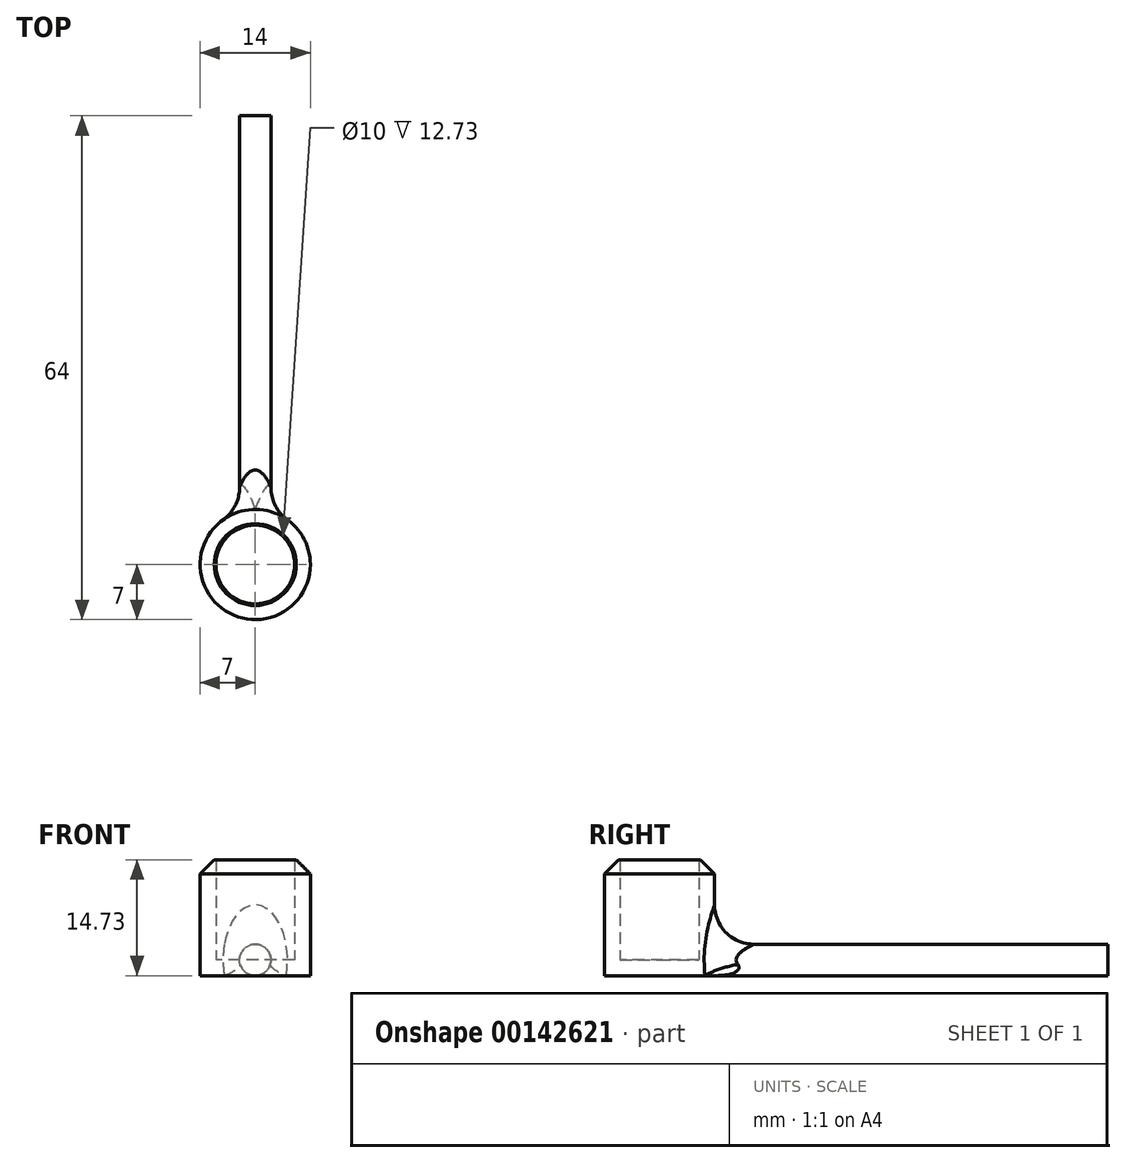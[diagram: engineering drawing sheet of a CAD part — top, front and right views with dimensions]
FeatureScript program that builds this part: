
annotation { "Feature Type Name" : "Feature", "Feature Type Description" : "" }
export const myFeature = defineFeature(function(context is Context, id is Id, definition is map)
    precondition{}
    {
        {
            var Q0;
            Q0=qCreatedBy(makeId("Top.planeOp"),FACE);
            var sketch = newSketch(context, id + "F0", { "sketchPlane" : qUnion([Q0])});
            skCircle(sketch, "E0", {"center": v(0, 0) * mm, "radius": 5 * mm});
            skCircle(sketch, "E1", {"center": v(0, 0) * mm, "radius": 7 * mm});
            skSolve(sketch);
        }
        {
            var Q0;
            Q0=makeQuery(id+"F0.imprint","IMPRINT",FACE,{"disambiguationData":[TD([[makeQuery(id+"F0.imprint","IMPRINT",EDGE,{"derivedFrom":sQuery(id+"F0.wireOp",EDGE,"E0")}),-1.0]])]});
            var Q1;
            Q1=makeQuery(id+"F0.imprint","IMPRINT",FACE,{"disambiguationData":[TD([[makeQuery(id+"F0.imprint","IMPRINT",EDGE,{"derivedFrom":sQuery(id+"F0.wireOp",EDGE,"E0")}),1.0]])]});
            extrude(context, id + "F1", {"entities" : qUnion([Q0, Q1]), "depth" : 2 * mm});
        }
        {
            var Q0;
            Q0=makeQuery(id+"F0.imprint","IMPRINT",FACE,{"disambiguationData":[TD([[makeQuery(id+"F0.imprint","IMPRINT",EDGE,{"derivedFrom":sQuery(id+"F0.wireOp",EDGE,"E0")}),-1.0]])]});
            extrude(context, id + "F2", {"entities" : qUnion([Q0]), "operationType" : NewBodyOperationType.ADD, "depth" : 14.73 * mm});
        }
        {
            var Q0;
            Q0=makeQuery(id+"F0.imprint","IMPRINT",FACE,{"disambiguationData":[TD([[makeQuery(id+"F0.imprint","IMPRINT",EDGE,{"derivedFrom":sQuery(id+"F0.wireOp",EDGE,"E0")}),1.0]])]});
            var sketch = newSketch(context, id + "F3", { "sketchPlane" : qUnion([Q0])});
            skLineSegment(sketch, "E2", {"start": v(0, 0) * mm, "end": v(0, 5) * mm});
            skLineSegment(sketch, "E3", {"start": v(0, 5) * mm, "end": v(0, 7) * mm});
            skLineSegment(sketch, "E4", {"start": v(0, 7) * mm, "end": v(10, 7) * mm});
            skSolve(sketch);
        }
        {
            var Q0;
            Q0=sQuery(id+"F3.wireOp",EDGE,"E4");
            cPlane(context, id + "F4", {"entities" : qUnion([Q0]), "cplaneType" : CPlaneType.LINE_ANGLE, "offset" : 25 * mm, "angle" : 0 * degree, "width" : 150 * mm, "height" : 150 * mm});
        }
        {
            var Q0;
            Q0=qCreatedBy(id+"F4.planeOp",FACE);
            var sketch = newSketch(context, id + "F5", { "sketchPlane" : qUnion([Q0])});
            skLineSegment(sketch, "E5", {"start": v(0, 0) * mm, "end": v(0, 2) * mm});
            skCircle(sketch, "E6", {"center": v(0, 2) * mm, "radius": 2 * mm});
            skSolve(sketch);
        }
        {
            var Q0;
            Q0=makeQuery(id+"F5.imprint","IMPRINT",FACE,{"disambiguationData":[TD([[makeQuery(id+"F5.imprint","IMPRINT",EDGE,{"derivedFrom":sQuery(id+"F5.wireOp",EDGE,"E6")}),1.0]])]});
            extrude(context, id + "F6", {"entities" : qUnion([Q0]), "operationType" : NewBodyOperationType.ADD, "oppositeDirection" : true, "depth" : 1 * mm});
        }
        {
            var Q0;
            Q0=makeQuery(id+"F6.opExtrude","CAP_FACE",FACE,{"disambiguationData":[OSD([sQuery(id+"F5.wireOp",EDGE,"E6")])],"isStart":true});
            extrude(context, id + "F7", {"entities" : qUnion([Q0]), "operationType" : NewBodyOperationType.ADD, "depth" : 50 * mm});
        }
        {
            var Q0;
            Q0=makeQuery(id+"F2.opExtrude","CAP_EDGE",EDGE,{"disambiguationData":[OSD([sQuery(id+"F0.wireOp",EDGE,"E1")])],"isStart":false});
            chamfer(context, id + "F8", {"entities" : qUnion([Q0]), "width" : 1.8 * mm, "tangentPropagation" : true});
        }
        {
            var Q0;
            {var subQ0=makeQuery(id+"F6.opExtrude","SWEPT_FACE",FACE,{"disambiguationData":[OSD([sQuery(id+"F5.wireOp",EDGE,"E6")])]});var subQ1=sQuery(id+"F0.wireOp",EDGE,"E1");var subQ2=makeQuery(id+"F2.boolean.opBoolean","MERGE",FACE,{"derivedFrom":[makeQuery(id+"F1.opExtrude","SWEPT_FACE",FACE,{"disambiguationData":[OSD([subQ1])]}),makeQuery(id+"F2.opExtrude","SWEPT_FACE",FACE,{"disambiguationData":[OSD([subQ1])]})]});Q0=makeQuery(id+"F7.boolean.opBoolean","MERGE",EDGE,{"derivedFrom":[makeQuery(id+"F6.boolean.opBoolean","INTERSECT",EDGE,{"disambiguationData":[OD(0.0)],"derivedFrom":[subQ2,subQ0]}),makeQuery(id+"F6.boolean.opBoolean","INTERSECT",EDGE,{"disambiguationData":[OD(1.0)],"derivedFrom":[subQ2,subQ0]})]});}
            fillet(context, id + "F9", {"entities" : qUnion([Q0]), "radius" : 5 * mm, "tangentPropagation" : true, "allowEdgeOverflow" : false});
        }
    });
